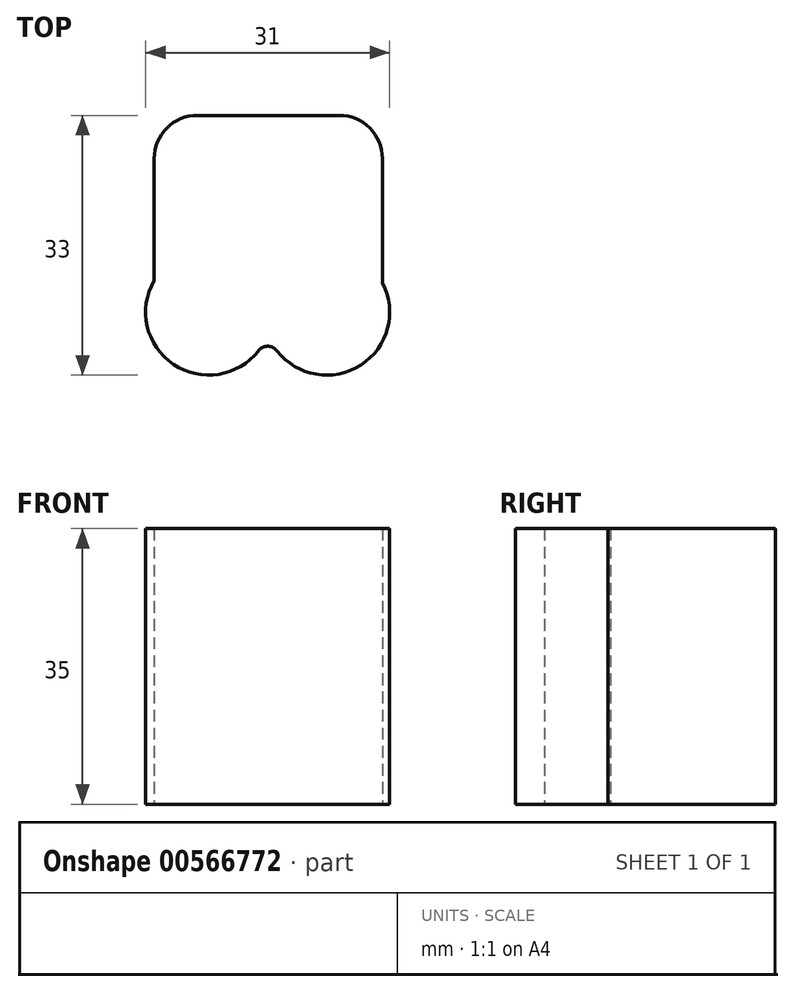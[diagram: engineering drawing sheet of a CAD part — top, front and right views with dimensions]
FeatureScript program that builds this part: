
annotation { "Feature Type Name" : "Feature", "Feature Type Description" : "" }
export const myFeature = defineFeature(function(context is Context, id is Id, definition is map)
    precondition{}
    {
        {
            var Q0;
            Q0=qCreatedBy(makeId("Top.planeOp"),FACE);
            var sketch = newSketch(context, id + "F0", { "sketchPlane" : qUnion([Q0])});
            skPoint(sketch, "E0.visualSharp", {"position": v(-14, 17) * mm});
            skPoint(sketch, "E1.visualSharp", {"position": v(13.56, 17) * mm});
            skArc(sketch, "E2.filletArc", {"start": v(1.5, -12.1) * mm, "mid": v(-0.08, -11.33) * mm, "end": v(-1.66, -12.1) * mm});
            skArc(sketch, "E3.0", {"start": v(-9, 17.5) * mm, "mid": v(-12.89, 15.89) * mm, "end": v(-14.5, 12) * mm});
            skLineSegment(sketch, "E3.1", {"start": v(-9, 17.5) * mm, "end": v(9, 17.5) * mm});
            skLineSegment(sketch, "E3.2", {"start": v(-14.5, 12) * mm, "end": v(-14.5, -3.48) * mm});
            skArc(sketch, "E3.3", {"start": v(14.5, 12) * mm, "mid": v(12.89, 15.89) * mm, "end": v(9, 17.5) * mm});
            skArc(sketch, "E3.4", {"start": v(-14.5, -3.48) * mm, "mid": v(-12.06, -14.13) * mm, "end": v(-1.27, -12.41) * mm});
            skArc(sketch, "E3.5", {"start": v(1.1, -12.41) * mm, "mid": v(-0.08, -11.83) * mm, "end": v(-1.27, -12.41) * mm});
            skArc(sketch, "E3.6", {"start": v(1.1, -12.41) * mm, "mid": v(11.75, -14.23) * mm, "end": v(14.5, -3.78) * mm});
            skLineSegment(sketch, "E3.7", {"start": v(14.5, 12) * mm, "end": v(14.5, -3.78) * mm});
            skSolve(sketch);
        }
        {
            var Q0;
            Q0 = qSketchRegion(id + "F0", true);
            extrude(context, id + "F1", {"entities" : qUnion([Q0]), "depth" : 35 * mm, "offsetDistance" : 25 * mm});
        }
    });
